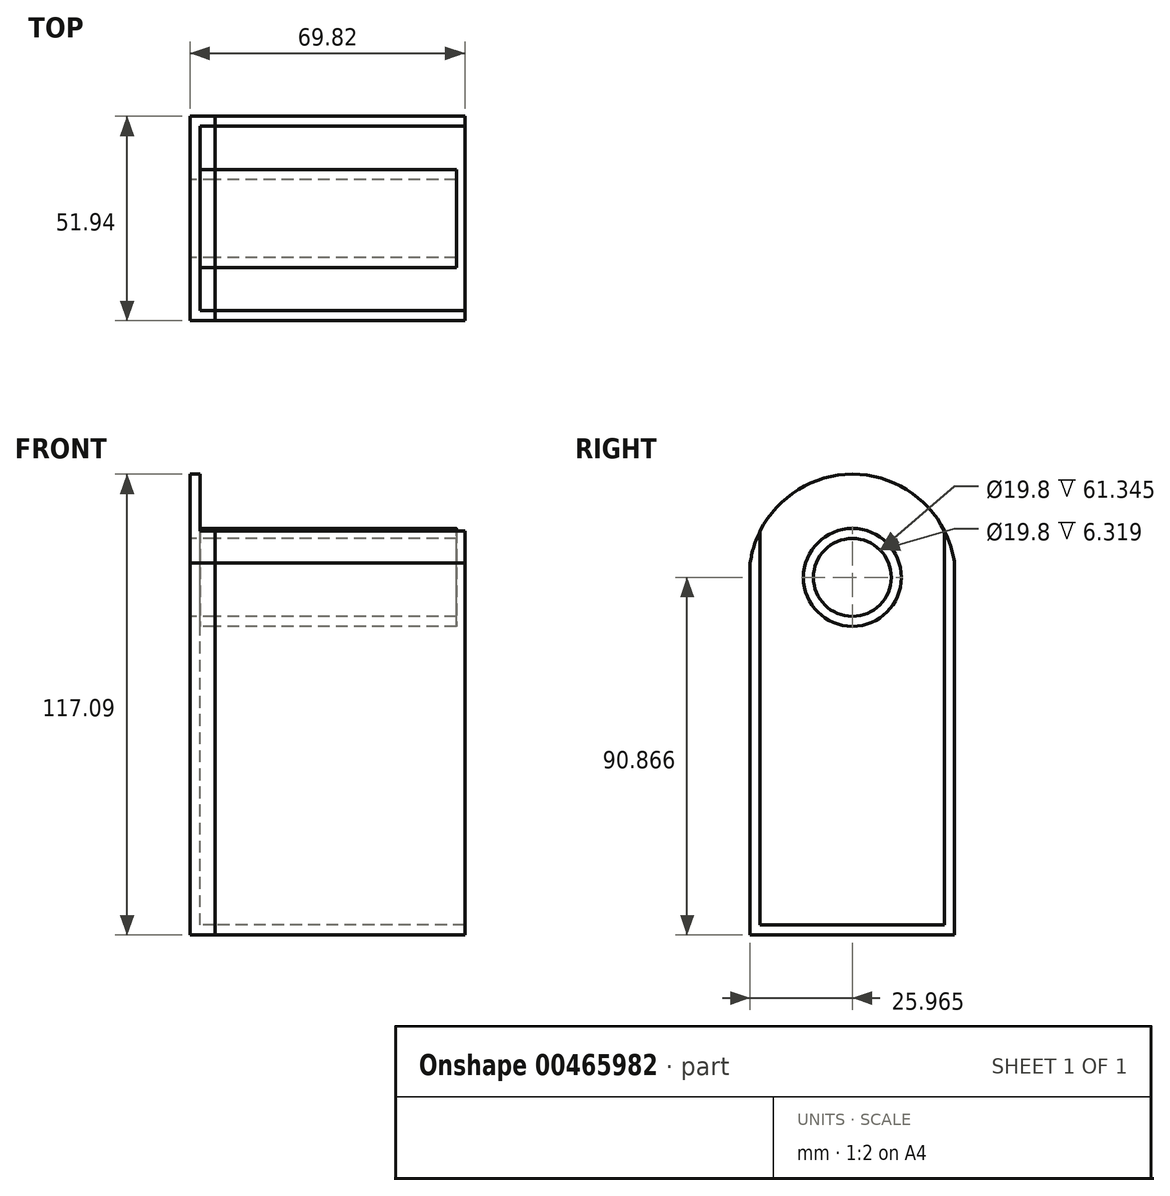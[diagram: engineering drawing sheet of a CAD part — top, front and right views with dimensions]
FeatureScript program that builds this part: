
annotation { "Feature Type Name" : "Feature", "Feature Type Description" : "" }
export const myFeature = defineFeature(function(context is Context, id is Id, definition is map)
    precondition{}
    {
        {
            var Q0;
            Q0=qCreatedBy(makeId("Right.planeOp"),FACE);
            var sketch = newSketch(context, id + "F0", { "sketchPlane" : qUnion([Q0])});
            skLineSegment(sketch, "E0", {"start": v(0, 115.46) * mm, "end": v(0, -108.87) * mm, "construction": true});
            skLineSegment(sketch, "E1.bottom", {"start": v(25.97, -58.08) * mm, "end": v(-25.97, -58.08) * mm});
            skLineSegment(sketch, "E1.left", {"start": v(25.97, -58.08) * mm, "end": v(25.97, 36.35) * mm});
            skLineSegment(sketch, "E1.right", {"start": v(-25.97, -58.08) * mm, "end": v(-25.97, 36.42) * mm});
            skPoint(sketch, "E1.middle", {"position": v(0, 0) * mm});
            skArc(sketch, "E2", {"start": v(25.97, 36.35) * mm, "mid": v(0.03, 59) * mm, "end": v(-25.97, 36.42) * mm});
            skPoint(sketch, "E3.orphan", {"position": v(-25.97, 58.08) * mm});
            skPoint(sketch, "E4.orphan", {"position": v(25.97, 58.08) * mm});
            skCircle(sketch, "E5", {"center": v(0, 32.79) * mm, "radius": 9.9 * mm});
            skSolve(sketch);
        }
        {
            var Q0;
            Q0=makeQuery(id+"F0.imprint","IMPRINT",FACE,{"disambiguationData":[TD([[makeQuery(id+"F0.imprint","IMPRINT",EDGE,{"derivedFrom":sQuery(id+"F0.wireOp",EDGE,"E1.bottom")}),-1.0]])]});
            extrude(context, id + "F1", {"entities" : qUnion([Q0]), "depth" : 6.32 * mm});
        }
        {
            var Q0;
            Q0=makeQuery(id+"F1.opExtrude","SWEPT_FACE",FACE,{"disambiguationData":[OSD([sQuery(id+"F0.wireOp",EDGE,"E2")])]});
            var Q1;
            Q1=makeQuery(id+"F1.opExtrude","CAP_FACE",FACE,{"disambiguationData":[OSD([sQuery(id+"F0.wireOp",EDGE,"E1.bottom"),sQuery(id+"F0.wireOp",EDGE,"E1.left"),sQuery(id+"F0.wireOp",EDGE,"E1.right"),sQuery(id+"F0.wireOp",EDGE,"E2"),sQuery(id+"F0.wireOp",EDGE,"E5")])],"isStart":false});
            shell(context, id + "F2", {"entities" : qUnion([Q0, Q1]), "thickness" : 2.54 * mm});
        }
        {
            var Q0;
            Q0=makeQuery(id+"F1.opExtrude","CAP_FACE",FACE,{"disambiguationData":[OSD([sQuery(id+"F0.wireOp",EDGE,"E1.bottom"),sQuery(id+"F0.wireOp",EDGE,"E1.left"),sQuery(id+"F0.wireOp",EDGE,"E1.right"),sQuery(id+"F0.wireOp",EDGE,"E2"),sQuery(id+"F0.wireOp",EDGE,"E5")])],"isStart":false});
            extrude(context, id + "F3", {"entities" : qUnion([Q0]), "depth" : 63.5 * mm});
        }
        {
            var Q0;
            {var subQ0=sQuery(id+"F0.wireOp",EDGE,"E5");var subQ1=sQuery(id+"F0.wireOp",EDGE,"E2");var subQ2=sQuery(id+"F0.wireOp",EDGE,"E1.right");var subQ3=sQuery(id+"F0.wireOp",EDGE,"E1.left");var subQ4=sQuery(id+"F0.wireOp",EDGE,"E1.bottom");Q0=makeQuery(id+"F2.opShell","OFFSET_FACE",FACE,{"disambiguationData":[OSD([subQ4,subQ3,subQ2,subQ1,subQ0]),TDD([makeQuery(id+"F1.opExtrude","CAP_FACE",FACE,{"disambiguationData":[OSD([subQ4,subQ3,subQ2,subQ1,subQ0])],"isStart":false})])]});}
            extrude(context, id + "F4", {"entities" : qUnion([Q0]), "depth" : 61.35 * mm});
        }
    });
